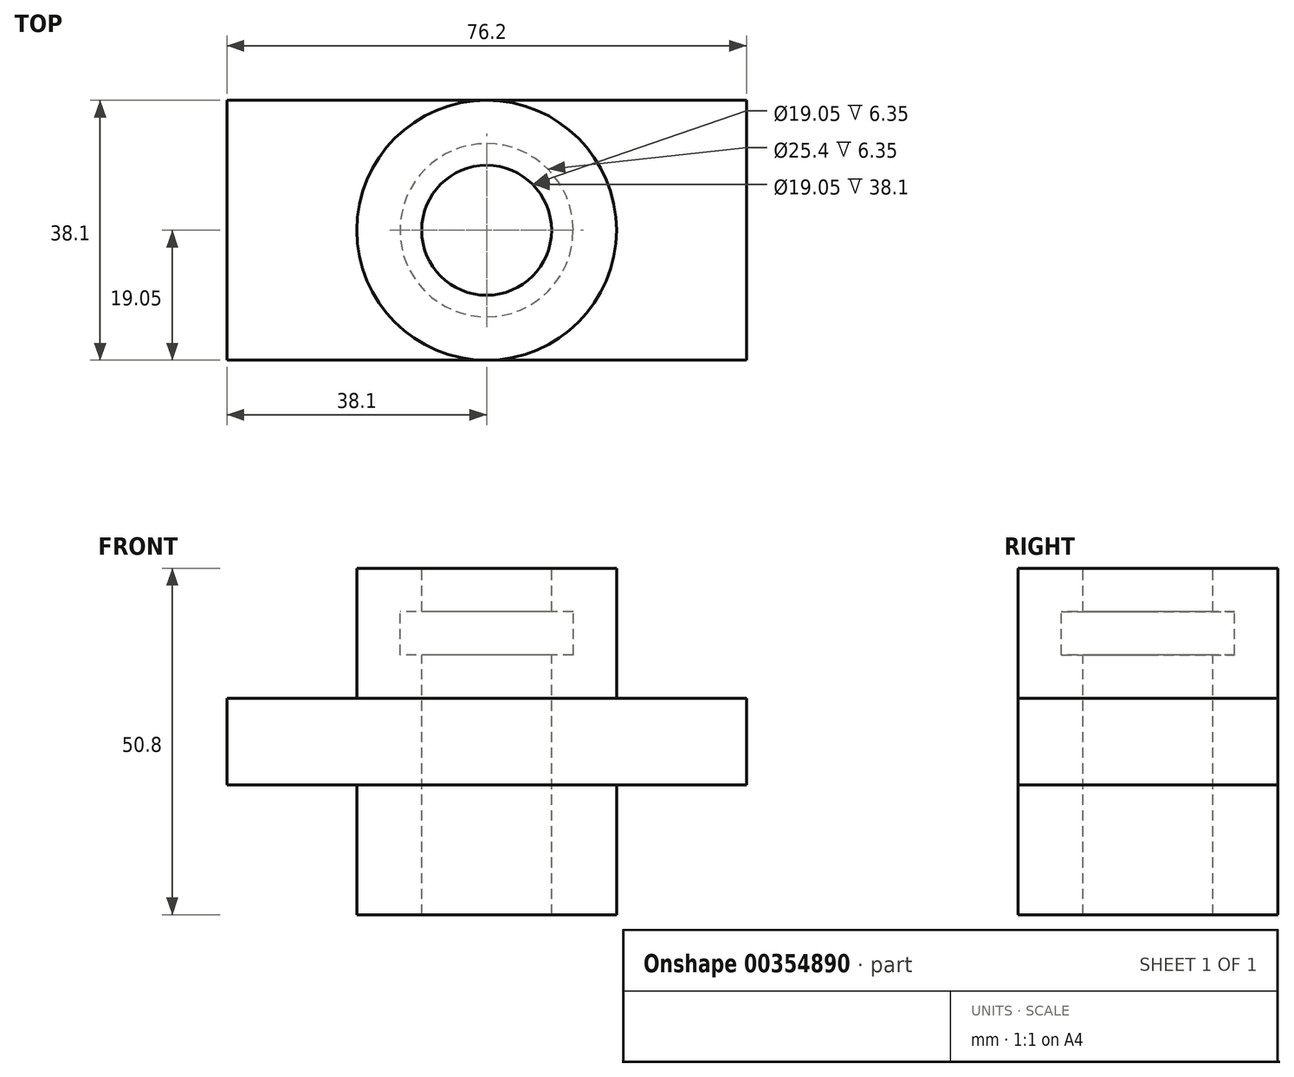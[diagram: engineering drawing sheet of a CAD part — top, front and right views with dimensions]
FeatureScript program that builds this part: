
annotation { "Feature Type Name" : "Feature", "Feature Type Description" : "" }
export const myFeature = defineFeature(function(context is Context, id is Id, definition is map)
    precondition{}
    {
        {
            var Q0;
            Q0=qCreatedBy(makeId("Top.planeOp"),FACE);
            var sketch = newSketch(context, id + "F0", { "sketchPlane" : qUnion([Q0])});
            skCircle(sketch, "E0", {"center": v(0, 0) * mm, "radius": 19.05 * mm});
            skSolve(sketch);
        }
        {
            var Q0;
            Q0=makeQuery(id+"F0.imprint","IMPRINT",FACE,{"disambiguationData":[TD([[makeQuery(id+"F0.imprint","IMPRINT",EDGE,{"derivedFrom":sQuery(id+"F0.wireOp",EDGE,"E0")}),1.0]])]});
            extrude(context, id + "F1", {"entities" : qUnion([Q0]), "endBound" : BoundingType.SYMMETRIC, "depth" : 50.8 * mm});
        }
        {
            var Q0;
            Q0=makeQuery(id+"F1.opExtrude","CAP_FACE",FACE,{"disambiguationData":[OSD([sQuery(id+"F0.wireOp",EDGE,"E0")])],"isStart":false});
            var sketch = newSketch(context, id + "F2", { "sketchPlane" : qUnion([Q0])});
            skCircle(sketch, "E1", {"center": v(0, 0) * mm, "radius": 9.53 * mm});
            skSolve(sketch);
        }
        {
            var Q0;
            Q0 = qSketchRegion(id + "F2", true);
            extrude(context, id + "F3", {"entities" : qUnion([Q0]), "operationType" : NewBodyOperationType.REMOVE, "oppositeDirection" : true, "depth" : 6.35 * mm});
        }
        {
            var Q0;
            Q0=makeQuery(id+"F3.boolean.opBoolean","COPY",FACE,{"derivedFrom":makeQuery(id+"F3.opExtrude","CAP_FACE",FACE,{"disambiguationData":[OSD([sQuery(id+"F2.wireOp",EDGE,"E1")])],"isStart":false})});
            var sketch = newSketch(context, id + "F4", { "sketchPlane" : qUnion([Q0])});
            skCircle(sketch, "E2", {"center": v(0, 0) * mm, "radius": 12.7 * mm});
            skSolve(sketch);
        }
        {
            var Q0;
            Q0 = qSketchRegion(id + "F4", true);
            extrude(context, id + "F5", {"entities" : qUnion([Q0]), "operationType" : NewBodyOperationType.REMOVE, "oppositeDirection" : true, "depth" : 6.35 * mm});
        }
        {
            var Q0;
            Q0=makeQuery(id+"F5.boolean.opBoolean","COPY",FACE,{"derivedFrom":makeQuery(id+"F5.opExtrude","CAP_FACE",FACE,{"disambiguationData":[OSD([sQuery(id+"F4.wireOp",EDGE,"E2")])],"isStart":false})});
            var sketch = newSketch(context, id + "F6", { "sketchPlane" : qUnion([Q0])});
            skCircle(sketch, "E3", {"center": v(0, 0) * mm, "radius": 9.53 * mm});
            skSolve(sketch);
        }
        {
            var Q0;
            Q0 = qSketchRegion(id + "F6", true);
            extrude(context, id + "F7", {"entities" : qUnion([Q0]), "operationType" : NewBodyOperationType.REMOVE, "endBound" : BoundingType.THROUGH_ALL, "oppositeDirection" : true, "depth" : 25.4 * mm});
        }
        {
            var Q0;
            Q0=qCreatedBy(makeId("Right.planeOp"),FACE);
            var sketch = newSketch(context, id + "F8", { "sketchPlane" : qUnion([Q0])});
            skLineSegment(sketch, "E4.bottom", {"start": v(-19.05, 6.35) * mm, "end": v(19.05, 6.35) * mm});
            skLineSegment(sketch, "E4.top", {"start": v(-19.05, -6.35) * mm, "end": v(19.05, -6.35) * mm});
            skLineSegment(sketch, "E4.left", {"start": v(-19.05, 6.35) * mm, "end": v(-19.05, -6.35) * mm});
            skLineSegment(sketch, "E4.right", {"start": v(19.05, 6.35) * mm, "end": v(19.05, -6.35) * mm});
            skSolve(sketch);
        }
        {
            var Q0;
            Q0 = qSketchRegion(id + "F8", true);
            extrude(context, id + "F9", {"entities" : qUnion([Q0]), "operationType" : NewBodyOperationType.ADD, "endBound" : BoundingType.SYMMETRIC, "depth" : 76.2 * mm});
        }
        {
            var Q0;
            Q0=makeQuery(id+"F9.boolean.opBoolean","SPLIT",FACE,{"disambiguationData":[TD([makeQuery(id+"F7.boolean.opBoolean","COPY",FACE,{"derivedFrom":makeQuery(id+"F7.opExtrude","SWEPT_FACE",FACE,{"disambiguationData":[OSD([sQuery(id+"F6.wireOp",EDGE,"E3")])]})})])],"derivedFrom":makeQuery(id+"F9.opExtrude","SWEPT_FACE",FACE,{"disambiguationData":[OSD([sQuery(id+"F8.wireOp",EDGE,"E4.bottom")])]})});
            extrude(context, id + "F10", {"entities" : qUnion([Q0]), "operationType" : NewBodyOperationType.REMOVE, "endBound" : BoundingType.THROUGH_ALL, "oppositeDirection" : true, "depth" : 25.4 * mm});
        }
    });
